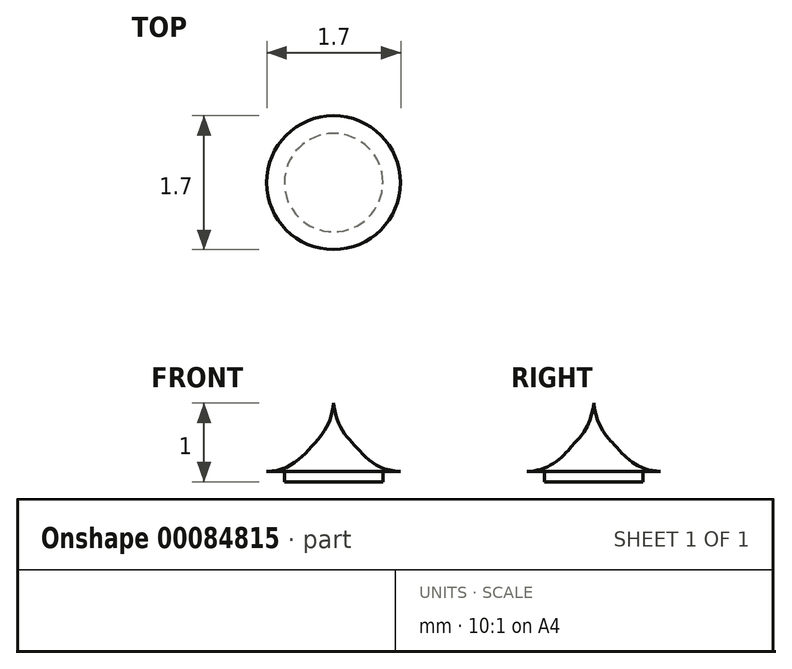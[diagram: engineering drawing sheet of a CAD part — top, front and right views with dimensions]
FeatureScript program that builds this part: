
annotation { "Feature Type Name" : "Feature", "Feature Type Description" : "" }
export const myFeature = defineFeature(function(context is Context, id is Id, definition is map)
    precondition{}
    {
        {
            var Q0;
            Q0=qCreatedBy(makeId("Front.planeOp"),FACE);
            var sketch = newSketch(context, id + "F0", { "sketchPlane" : qUnion([Q0])});
            skLineSegment(sketch, "E0", {"start": v(-29.29, 27.92) * mm, "end": v(-17.25, 27.92) * mm, "construction": true});
            skLineSegment(sketch, "E1", {"start": v(-22.38, 29.2) * mm, "end": v(-22.38, 26.36) * mm, "construction": true});
            skLineSegment(sketch, "E2", {"start": v(-23, 27.92) * mm, "end": v(-22.38, 27.92) * mm});
            skLineSegment(sketch, "E3", {"start": v(-22.38, 27.92) * mm, "end": v(-21.76, 27.92) * mm});
            skPoint(sketch, "E4.visualSharp", {"position": v(-23, 27.83) * mm});
            skPoint(sketch, "E5.MirrorCS.end.orphan", {"position": v(-22.38, 28.16) * mm});
            skLineSegment(sketch, "E6", {"start": v(-21.76, 27.92) * mm, "end": v(-21.76, 28.05) * mm});
            skLineSegment(sketch, "E7", {"start": v(-21.76, 28.05) * mm, "end": v(-21.53, 28.05) * mm});
            skFitSpline(sketch, "E8", {"points": [v(-21.53, 28.05) * mm, v(-22.1, 28.37) * mm, v(-22.38, 28.92) * mm], "startDerivative": vector(-1.77, 0.04) * mm, "endDerivative": vector(-0.2, 1.8) * mm});
            skFitSpline(sketch, "E9.MirrorCS", {"points": [v(-23.23, 28.05) * mm, v(-22.66, 28.37) * mm, v(-22.38, 28.92) * mm], "startDerivative": vector(1.77, 0.04) * mm, "endDerivative": vector(0.2, 1.8) * mm});
            skLineSegment(sketch, "E10.MirrorCS", {"start": v(-23, 28.05) * mm, "end": v(-23.23, 28.05) * mm});
            skLineSegment(sketch, "E11.MirrorCS", {"start": v(-23, 27.92) * mm, "end": v(-23, 28.05) * mm});
            skLineSegment(sketch, "E12", {"start": v(-22.38, 27.92) * mm, "end": v(-22.38, 28.92) * mm});
            skSolve(sketch);
        }
        {
            var Q0;
            Q0=makeQuery(id+"F0.imprint","IMPRINT",FACE,{"disambiguationData":[TD([[makeQuery(id+"F0.imprint","IMPRINT",EDGE,{"derivedFrom":sQuery(id+"F0.wireOp",EDGE,"E3")}),1.0]])]});
            var Q1;
            Q1=sQuery(id+"F0.wireOp",EDGE,"E1");
            revolve(context, id + "F1", {"entities" : qUnion([Q0]), "axis" : qUnion([Q1]), "revolveType" : RevolveType.FULL});
        }
    });
